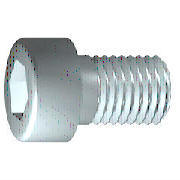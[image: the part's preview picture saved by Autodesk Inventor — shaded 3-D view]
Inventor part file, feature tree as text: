
AUTODESK INVENTOR PART (.ipt)
format: ipt  version: 2020 (Build 240168000, 168)  size: 195,584 bytes
history: native  units: mm (DEFAULTED — no unit token found)
features: sketch x2, extrude x1, plane x1, fillet x1
ambient origin geometry x7: Origin, YZ Plane, XY Plane, X Axis, Y Axis, Z Axis, Center Point
bodies: Solid1 (feature_tree)
feature tree (5):
  extrude  "슬롯"  Depth=21.25mm
  plane  "Work Plane1"
  fillet  "Fillet2"  Radius=0.920275mm
  sketch  "스케치1"
  sketch  "스케치2"
